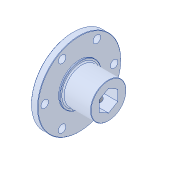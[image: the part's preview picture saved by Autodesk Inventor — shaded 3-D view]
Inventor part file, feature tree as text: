
AUTODESK INVENTOR PART (.ipt)
format: ipt  version: 2018 (Build 220112000, 112)  size: 156,672 bytes
history: native  units: in
note: dims shown in document units (in); Inventor stores cm internally (conversion verified against a paired STEP export)
features: hole x1, sketch x1, chamfer x1
ambient origin geometry x8: Origin, YZ Plane, XZ Plane, XY Plane, X Axis, Y Axis, Z Axis, Center Point
bodies: Solid1 (feature_tree)
feature tree (3):
  hole  "Hole1"  [1 undecoded]
  sketch  "Sketch1"  dims[d0=0.375in d1=0.163in d2=0.394in d3=0.375in d4=0.25in d5=0.5635in d6=0.559in d7=0.8108in]
  chamfer  "Chamfer3"  [1 undecoded]
note: 2 required parameter values undecoded (feature->parameter linkage not recoverable at this tier; creation-order binding heuristic only, values carry confidence <= 0.55)
